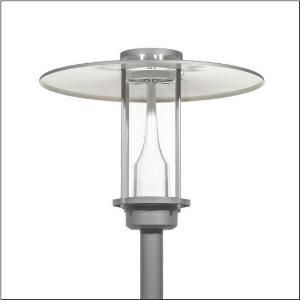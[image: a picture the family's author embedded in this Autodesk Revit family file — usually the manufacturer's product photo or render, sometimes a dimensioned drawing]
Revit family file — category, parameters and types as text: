
# Revit family: city-light_plus_iq___p1_0a_5xa5275lf14hp_bc32
name_source: partatom
category: Lighting Fixtures
units: mm (PartAtom-declared; Revit-internal decimal feet)

## family parameters
Cut with Voids When Loaded = No
Host = Face
Light Source = No
Part Type = Normal
Room Calculation Point = No
Round Connector Dimension = Use Diameter
Shared = No

## types (1)
- --- (1 x LED, 4680 lm, 33.6 W, 4000K)
    Apparent Load = 34 VA
    CIE Flux Codes = 30 60 90 96 100
    Color Rendering = 70
    Color Temperature = 4000K
    Default Elevation = 1800 mm
    Description = City-Light Plus iQ, mast luminaire, Module 540 iQ-SR, primary light control with 3 zone facetted reflector, of plastic, silver coated, highly specular, structured, primary optical cover: cover, of PMMA, transparent, light distribution: P1.0a, light emission: direct distribution, primary light characteristic: strongly asymmetric, installation type: post-top, LED, High Power LED, rated luminous flux: 4.680lm, luminous efficacy: 139lm/W, light colour: 740, colour temperature: 4000K, control gear: ECG iQ, control: presetting dimming logarithmic, Street-Remote, Auto-Match, Temp-Guard, Lumen-Switch, Night-Set, Smart-Wire, Light-Fading, Desk-Remote (wireless, voltage-free reading and setting of iQ features in the workshop via application-optimized NFC function/RFID function), optimised constant luminous flux control (CLO 2.0), with terminal, 6-pole, max. 2.5mm², mains connection: 230..240V, AC, 50/60Hz, start of lifetime: 34W, end of service life: 36W, reduction: 15W, luminaire housing, upper part, of glass-fibre reinforced polyester, coated, Siteco® metallic grey (DB 702S), diameter: 750mm, height: 590mm, spigot size: d x l = 76 x 70mm (post-top) | with reducer (optional accessory) 60 x 70mm, post-top mast mounting element, of diecast aluminium, coated, Siteco® metallic grey (DB 702S), Module 540 iQ-SR, traffic white (RAL 9016), equipment: Power, protection rating (complete): IP65, insulation class (complete): insulation class II (safety insulation), certification: CE, ENEC, VDE, packaging unit: 1 piece

Light Distribution: P1.0a
    Height = 590 mm
    Lamp = 1 x LED
    Lamp Light Flux = 4680 lm
    Lamp Power = 33.6 W
    Lamp count = 1
    Length = 750 mm
    Luminous efficacy = 139 lm/W
    Manufacturer = Siteco
    ModVariant = No
    Model = 5XA5275LF14HP
    Number of Poles = 1
    OnlyDefault = Yes
    Power Factor = 1
    Product Name = City-Light Plus iQ | P1.0a
    Product group = mast luminaire | pylon top
    ProductGroupID = 6100
    Protection Class = Protection class II
    Protection Degree = IP 65
    RLX_Detail_Level = 1
    RLX_Emergency_Light_Flux = 0 lm
    RLX_Emergency_Type = 0
    RLX_Emergency_Type_DB = No
    RlxData = <blob elided: 52573 chars, md5=bc3b1ce0>
    Socket = socket
    Standby Power = 0 W
    System Light Flux = 4680 lm
    System Power = 34 W
    Type Comments = factory setting: luminous flux: 100 % | dim-lin: 254 | 695 mA
    Type Image = l_1006456.jpg
    URL = http://relux.com
    VarID = @adj_146341
    Voltage = 0 V
    Weight = 0.00 kg
    Width = 0 mm  [stored 0 ft]

note: [stored X ft] marks values corroborated as IEEE doubles in the binary element streams (Revit-internal decimal feet)

## geometry (parser evidence)
native form markers: Blend x4, Sweep x11
no freeform markers — native parametric forms only
